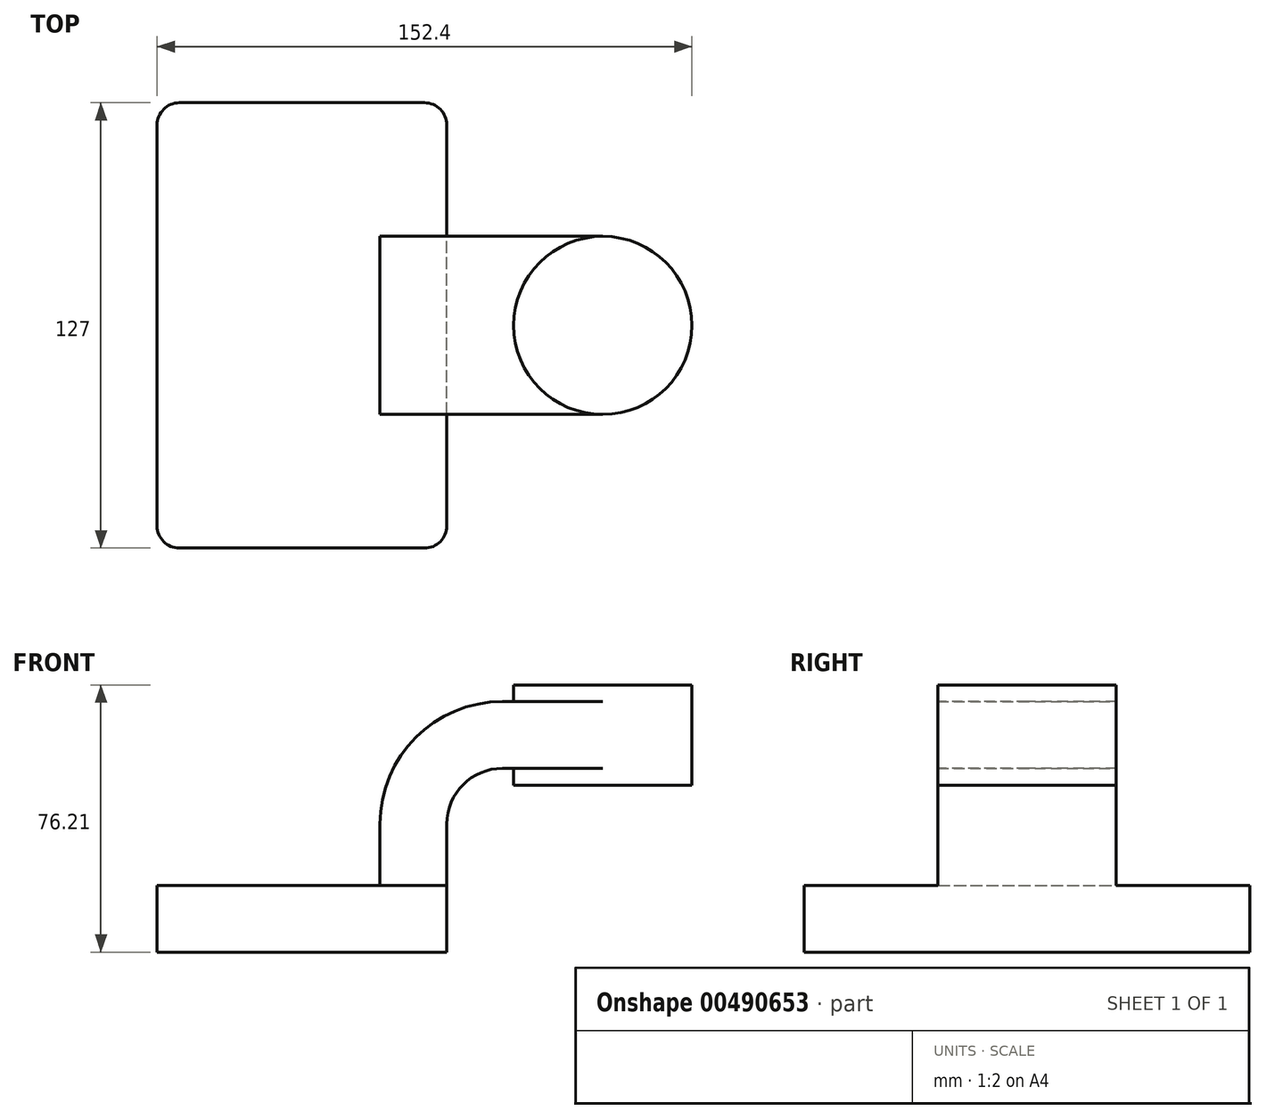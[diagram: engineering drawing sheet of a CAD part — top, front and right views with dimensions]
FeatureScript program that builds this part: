
annotation { "Feature Type Name" : "Feature", "Feature Type Description" : "" }
export const myFeature = defineFeature(function(context is Context, id is Id, definition is map)
    precondition{}
    {
        {
            var Q0;
            Q0=qCreatedBy(makeId("Front.planeOp"),FACE);
            var sketch = newSketch(context, id + "F0", { "sketchPlane" : qUnion([Q0])});
            skLineSegment(sketch, "E0.bottom", {"start": v(41.28, -9.52) * mm, "end": v(-41.28, -9.53) * mm});
            skLineSegment(sketch, "E0.top", {"start": v(41.28, 9.53) * mm, "end": v(-41.28, 9.53) * mm});
            skLineSegment(sketch, "E0.left", {"start": v(41.28, -9.52) * mm, "end": v(41.28, 9.53) * mm});
            skLineSegment(sketch, "E0.right", {"start": v(-41.28, -9.53) * mm, "end": v(-41.28, 9.53) * mm});
            skPoint(sketch, "E0.middle", {"position": v(0, 0) * mm});
            skLineSegment(sketch, "E1.bottom", {"start": v(111.12, 66.68) * mm, "end": v(60.32, 66.68) * mm});
            skLineSegment(sketch, "E1.top", {"start": v(111.12, 38.1) * mm, "end": v(60.32, 38.1) * mm});
            skLineSegment(sketch, "E1.left", {"start": v(111.12, 66.68) * mm, "end": v(111.12, 38.1) * mm});
            skLineSegment(sketch, "E1.right", {"start": v(60.32, 66.68) * mm, "end": v(60.32, 38.1) * mm});
            skPoint(sketch, "E1.middle", {"position": v(85.72, 52.39) * mm});
            skLineSegment(sketch, "E2", {"start": v(41.28, 9.53) * mm, "end": v(41.28, 27) * mm});
            skArc(sketch, "E3", {"start": v(41.27, 27) * mm, "mid": v(45.92, 38.23) * mm, "end": v(57.15, 42.88) * mm});
            skLineSegment(sketch, "E4", {"start": v(57.15, 42.88) * mm, "end": v(85.72, 42.88) * mm});
            skLineSegment(sketch, "E5.0", {"start": v(57.15, 61.93) * mm, "end": v(85.72, 61.93) * mm});
            skArc(sketch, "E5.1", {"start": v(22.23, 27) * mm, "mid": v(32.45, 51.7) * mm, "end": v(57.15, 61.93) * mm});
            skLineSegment(sketch, "E5.2", {"start": v(22.22, 9.53) * mm, "end": v(22.22, 27) * mm});
            skText(sketch, "E6", { "text": "Jesús David Mendoza\nAutomatización Industrial \n", "fontName": "Arimo-Italic.ttf"});
            skFitSpline(sketch, "E7", {"points": [v(-41.28, 9.53) * mm, v(57.15, 61.93) * mm], "startDerivative": vector(0.82, 77.66) * mm, "endDerivative": vector(128.12, 0) * mm});
            skLineSegment(sketch, "E8", {"start": v(85.72, 38.1) * mm, "end": v(85.72, 66.68) * mm});
            const initialGuessF0  = {"E6": [0.01351, -0.07641, 1, 0, 0.01118]};
            skSetInitialGuess(sketch, initialGuessF0);
            skSolve(sketch);
        }
        {
            var Q0;
            Q0=makeQuery(id+"F0.imprint","IMPRINT",FACE,{"disambiguationData":[TD([[makeQuery(id+"F0.imprint","IMPRINT",EDGE,{"derivedFrom":sQuery(id+"F0.wireOp",EDGE,"E0.bottom")}),-1.0]])]});
            extrude(context, id + "F1", {"entities" : qUnion([Q0]), "endBound" : BoundingType.SYMMETRIC, "depth" : 127 * mm});
        }
        {
            var Q0;
            {var subQ1=sQuery(id+"F0.wireOp",EDGE,"E2");Q0=makeQuery(id+"F0.imprint","IMPRINT",FACE,{"disambiguationData":[TD([[makeQuery(id+"F0.imprint","IMPRINT",EDGE,{"derivedFrom":subQ1}),1.0]])]});}
            var Q1;
            {var subQ0=sQuery(id+"F0.wireOp",EDGE,"E5.0");var subQ1=sQuery(id+"F0.wireOp",EDGE,"E1.right");var subQ2=makeQuery(id+"F0.imprint","INTERSECT",VERTEX,{"derivedFrom":[subQ1,subQ0]});Q1=makeQuery(id+"F0.imprint","IMPRINT",FACE,{"disambiguationData":[TD([[makeQuery(id+"F0.imprint","IMPRINT",EDGE,{"disambiguationData":[TD([[subQ2,-1.0]])],"derivedFrom":subQ1}),1.0]])]});}
            extrude(context, id + "F2", {"entities" : qUnion([Q0, Q1]), "operationType" : NewBodyOperationType.ADD, "endBound" : BoundingType.SYMMETRIC, "depth" : 50.8 * mm});
        }
        {
            var Q0;
            Q0=makeQuery(id+"F0.imprint","IMPRINT",FACE,{"disambiguationData":[TD([[makeQuery(id+"F0.imprint","IMPRINT",EDGE,{"derivedFrom":sQuery(id+"F0.wireOp",EDGE,"E5.1")}),1.0]])]});
            extrude(context, id + "F3", {"entities" : qUnion([Q0]), "operationType" : NewBodyOperationType.ADD, "endBound" : BoundingType.SYMMETRIC, "depth" : 15.88 * mm});
        }
        {
            var Q0;
            {var subQ4=sQuery(id+"F0.wireOp",EDGE,"E1.left");Q0=makeQuery(id+"F0.imprint","IMPRINT",FACE,{"disambiguationData":[TD([[makeQuery(id+"F0.imprint","IMPRINT",EDGE,{"derivedFrom":subQ4}),-1.0]])]});}
            var Q1;
            Q1=sQuery(id+"F0.wireOp",EDGE,"E8");
            revolve(context, id + "F4", {"operationType" : NewBodyOperationType.ADD, "entities" : qUnion([Q0]), "axis" : qUnion([Q1]), "revolveType" : RevolveType.FULL});
        }
        {
            var Q0;
            Q0=makeQuery(id+"F1.opExtrude","CAP_EDGE",EDGE,{"disambiguationData":[OSD([sQuery(id+"F0.wireOp",EDGE,"E0.right")])],"isStart":false});
            var Q1;
            Q1=makeQuery(id+"F1.opExtrude","CAP_EDGE",EDGE,{"disambiguationData":[OSD([sQuery(id+"F0.wireOp",EDGE,"E0.left")])],"isStart":false});
            var Q2;
            Q2=makeQuery(id+"F1.opExtrude","CAP_EDGE",EDGE,{"disambiguationData":[OSD([sQuery(id+"F0.wireOp",EDGE,"E0.left")])],"isStart":true});
            var Q3;
            Q3=makeQuery(id+"F1.opExtrude","CAP_EDGE",EDGE,{"disambiguationData":[OSD([sQuery(id+"F0.wireOp",EDGE,"E0.right")])],"isStart":true});
            fillet(context, id + "F5", {"entities" : qUnion([Q0, Q1, Q2, Q3]), "radius" : 6.35 * mm, "tangentPropagation" : true, "allowEdgeOverflow" : false});
        }
    });
